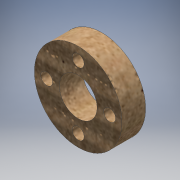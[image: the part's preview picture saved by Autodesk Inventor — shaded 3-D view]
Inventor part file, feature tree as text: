
AUTODESK INVENTOR PART (.ipt)
format: ipt  version: 2016 (Build 200138000, 138)  size: 155,648 bytes
history: native  units: mm
features: extrude x1, sketch x1
ambient origin geometry x8: Origin, YZ Plane, XZ Plane, XY Plane, X Axis, Y Axis, Z Axis, Center Point
bodies: Solid1 (feature_tree)
feature tree (2):
  extrude  "Extrusion1"  Depth=6.39mm
  sketch  "Sketch1"  dims[d0=22.098mm d1=3.0mm d2=7.9375mm d3=40.0mm d5=360.0deg d7=9.525mm d8=6.39mm d9=0.0mm]
